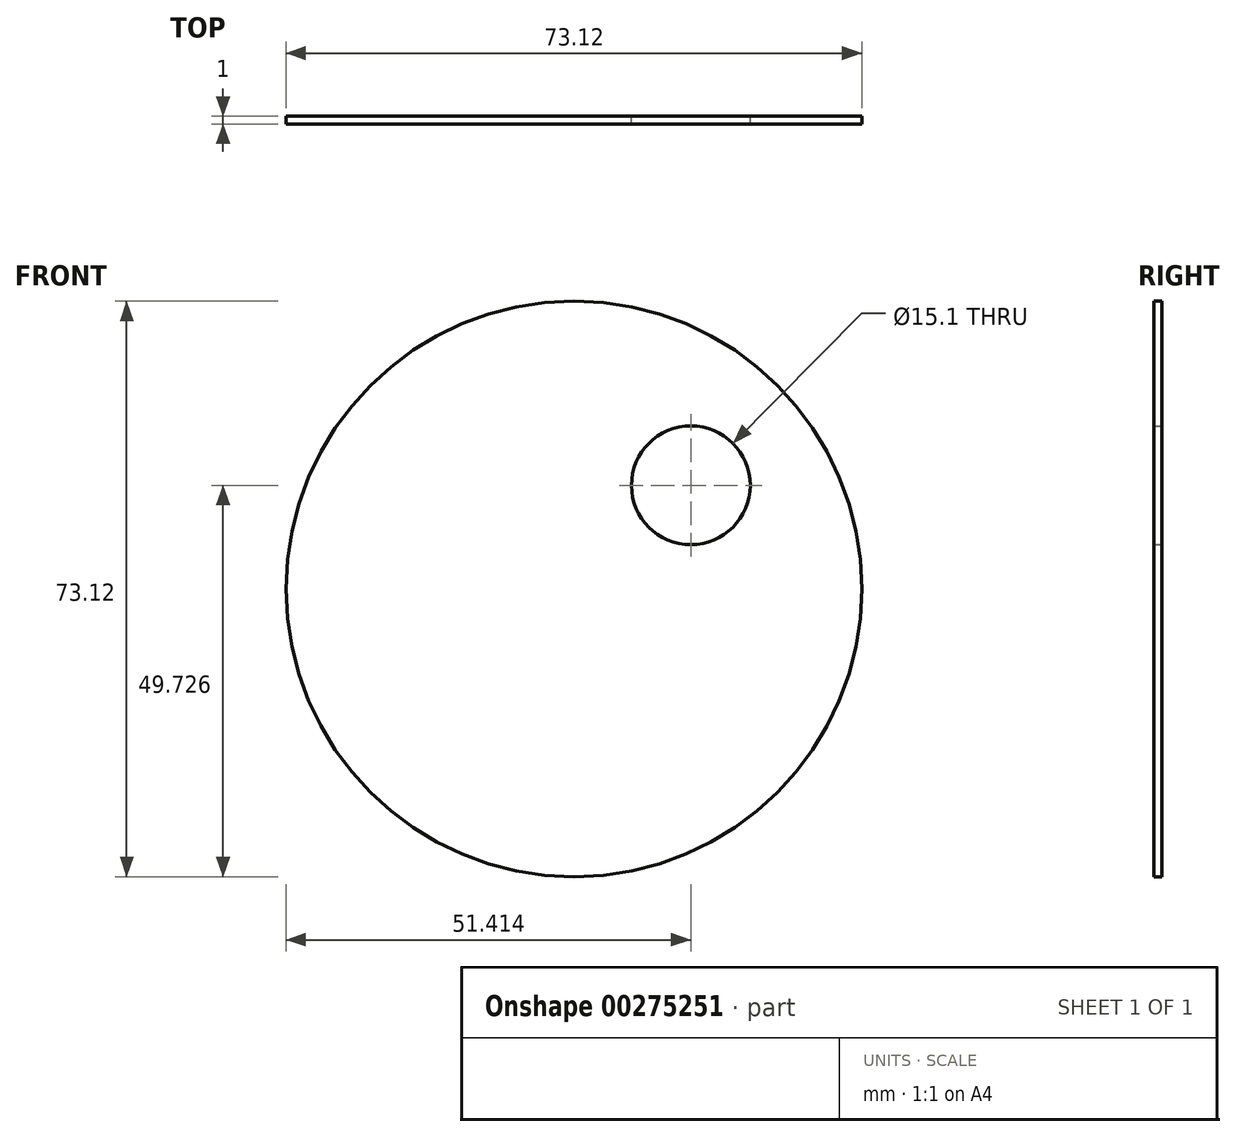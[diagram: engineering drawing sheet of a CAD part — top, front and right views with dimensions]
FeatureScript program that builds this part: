
annotation { "Feature Type Name" : "Feature", "Feature Type Description" : "" }
export const myFeature = defineFeature(function(context is Context, id is Id, definition is map)
    precondition{}
    {
        {
            var Q0;
            Q0=qCreatedBy(makeId("Front.planeOp"),FACE);
            var sketch = newSketch(context, id + "F0", { "sketchPlane" : qUnion([Q0])});
            skCircle(sketch, "E0", {"center": v(0, 0) * mm, "radius": 36.56 * mm});
            skCircle(sketch, "E1", {"center": v(14.85, 13.17) * mm, "radius": 7.55 * mm});
            skSolve(sketch);
        }
        {
            var Q0;
            Q0=makeQuery(id+"F0.imprint","IMPRINT",FACE,{"disambiguationData":[TD([[makeQuery(id+"F0.imprint","IMPRINT",EDGE,{"derivedFrom":sQuery(id+"F0.wireOp",EDGE,"E0")}),1.0]])]});
            extrude(context, id + "F1", {"entities" : qUnion([Q0]), "depth" : 1 * mm});
        }
    });
